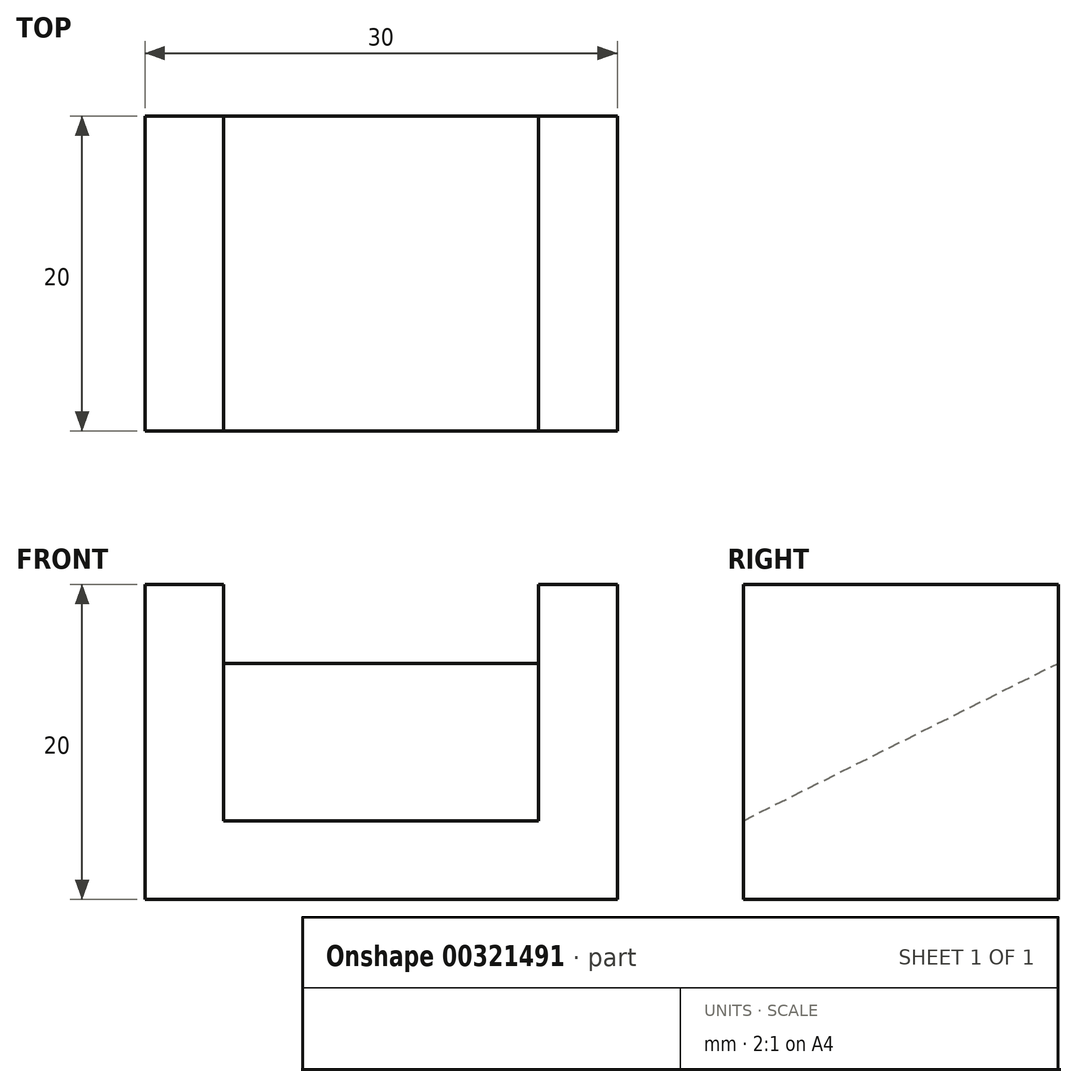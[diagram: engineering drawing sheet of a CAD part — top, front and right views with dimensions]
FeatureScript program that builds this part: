
annotation { "Feature Type Name" : "Feature", "Feature Type Description" : "" }
export const myFeature = defineFeature(function(context is Context, id is Id, definition is map)
    precondition{}
    {
        {
            var Q0;
            Q0=qCreatedBy(makeId("Right.planeOp"),FACE);
            var sketch = newSketch(context, id + "F0", { "sketchPlane" : qUnion([Q0])});
            skLineSegment(sketch, "E0", {"start": v(0, 0) * mm, "end": v(20, 0) * mm});
            skLineSegment(sketch, "E1", {"start": v(0, 0) * mm, "end": v(0, 5) * mm});
            skLineSegment(sketch, "E2", {"start": v(0, 5) * mm, "end": v(20, 5) * mm});
            skLineSegment(sketch, "E3", {"start": v(20, 5) * mm, "end": v(20, 0) * mm});
            skLineSegment(sketch, "E4", {"start": v(0, 5) * mm, "end": v(20, 15) * mm});
            skLineSegment(sketch, "E5", {"start": v(20, 15) * mm, "end": v(20, 5) * mm});
            skSolve(sketch);
        }
        {
            var Q0;
            Q0 = qSketchRegion(id + "F0", true);
            extrude(context, id + "F1", {"entities" : qUnion([Q0]), "depth" : 30 * mm});
        }
        {
            var Q0;
            Q0=makeQuery(id+"F1.opExtrude","CAP_FACE",FACE,{"disambiguationData":[OSD([sQuery(id+"F0.wireOp",EDGE,"E0"),sQuery(id+"F0.wireOp",EDGE,"E1"),sQuery(id+"F0.wireOp",EDGE,"E3"),sQuery(id+"F0.wireOp",EDGE,"E4"),sQuery(id+"F0.wireOp",EDGE,"E5")])],"isStart":false});
            var sketch = newSketch(context, id + "F2", { "sketchPlane" : qUnion([Q0])});
            skLineSegment(sketch, "E6", {"start": v(0, 5) * mm, "end": v(0, 20) * mm});
            skLineSegment(sketch, "E7", {"start": v(20, 15) * mm, "end": v(20, 20) * mm});
            skLineSegment(sketch, "E8", {"start": v(20, 20) * mm, "end": v(0, 20) * mm});
            skSolve(sketch);
        }
        {
            var Q0;
            Q0=makeQuery(id+"F2.imprint","IMPRINT",FACE,{"disambiguationData":[TD([[makeQuery(id+"F2.imprint","IMPRINT",EDGE,{"derivedFrom":sQuery(id+"F2.wireOp",EDGE,"E6")}),-1.0]])]});
            extrude(context, id + "F3", {"entities" : qUnion([Q0]), "operationType" : NewBodyOperationType.ADD, "oppositeDirection" : true, "depth" : 5 * mm});
        }
        {
            var Q0;
            Q0=makeQuery(id+"F1.opExtrude","CAP_FACE",FACE,{"disambiguationData":[OSD([sQuery(id+"F0.wireOp",EDGE,"E0"),sQuery(id+"F0.wireOp",EDGE,"E1"),sQuery(id+"F0.wireOp",EDGE,"E3"),sQuery(id+"F0.wireOp",EDGE,"E4"),sQuery(id+"F0.wireOp",EDGE,"E5")])],"isStart":true});
            var sketch = newSketch(context, id + "F4", { "sketchPlane" : qUnion([Q0])});
            skLineSegment(sketch, "E9", {"start": v(-20, 15) * mm, "end": v(-20, 20) * mm});
            skLineSegment(sketch, "E10", {"start": v(-20, 20) * mm, "end": v(0, 20) * mm});
            skLineSegment(sketch, "E11", {"start": v(0, 20) * mm, "end": v(0, 5) * mm});
            skSolve(sketch);
        }
        {
            var Q0;
            Q0=makeQuery(id+"F4.imprint","IMPRINT",FACE,{"disambiguationData":[TD([[makeQuery(id+"F4.imprint","IMPRINT",EDGE,{"derivedFrom":sQuery(id+"F4.wireOp",EDGE,"E9")}),-1.0]])]});
            extrude(context, id + "F5", {"entities" : qUnion([Q0]), "operationType" : NewBodyOperationType.ADD, "oppositeDirection" : true, "depth" : 5 * mm});
        }
    });
